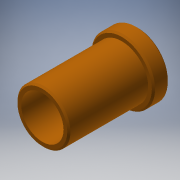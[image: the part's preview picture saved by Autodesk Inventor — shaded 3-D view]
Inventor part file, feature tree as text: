
AUTODESK INVENTOR PART (.ipt)
format: ipt  version: 2018 (Build 220112000, 112)  size: 126,464 bytes
history: native  units: mm
features: revolve x1, chamfer x1, sketch x1
ambient origin geometry x8: Origin, YZ Plane, XZ Plane, XY Plane, X Axis, Y Axis, Z Axis, Center Point
bodies: Solid1 (feature_tree)
feature tree (3):
  revolve  "Revolution1"  [1 undecoded]
  chamfer  "Chamfer1"  Distance=2.5mm
  sketch  "Sketch1"  dims[d0=9.0mm d1=2.0mm d2=2.5mm d3=3.0mm d4=1.5mm d5=9.0mm d6=90.0deg d7=0.15mm d8=2.0mm d9=45.0deg]
note: 1 required parameter value undecoded (feature->parameter linkage not recoverable at this tier; creation-order binding heuristic only, values carry confidence <= 0.55)
